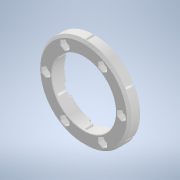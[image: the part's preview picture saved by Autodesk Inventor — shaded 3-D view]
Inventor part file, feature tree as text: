
AUTODESK INVENTOR PART (.ipt)
format: ipt  version: 2020 (Build 240168000, 168)  size: 4,947,968 bytes
history: native  units: in
note: dims shown in document units (in); Inventor stores cm internally (conversion verified against a paired STEP export)
features: extrude x5, sketch x5, other x4, chamfer x2, reference x2, imported_body x1, boolean_combine x1
ambient origin geometry x8: Origin, YZ Plane, XZ Plane, XY Plane, X Axis, Y Axis, Z Axis, Center Point
bodies: Solid1 (feature_tree), Solid2 (feature_tree)
feature tree (20):
  extrude  "Extrusion1"  Depth=0.7in TaperAngle=0.0deg
  extrude  "Extrusion2"  Depth=2.3622in TaperAngle=360.0deg
  imported_body  "Base1"
  boolean_combine  "Combine1"
  extrude  "Extrusion3"  Depth=0.4375in
  extrude  "Extrusion4"  Depth=0.3in TaperAngle=0.0deg
  extrude  "Extrusion5"  Depth=0.0118in TaperAngle=0.0deg
  chamfer  "Chamfer1"  Distance=2.3622in Angle=360.0deg
  chamfer  "Chamfer2"  Distance=0.0118in
  sketch  "Sketch1"  dims[d0=3.5in d2=0.7in d3=0.0in]
  reference  "Reference1"
  sketch  "Sketch2"  dims[d4=0.2656in d5=2.3622in d7=360.0deg]
  reference  "Reference2"
  sketch  "Sketch3"  dims[d9=0.0in d10=0.0in d11=0.4375in]
  sketch  "Sketch4"  dims[d12=2.3622in d14=360.0deg d16=0.3in d17=0.0in]
  sketch  "Sketch5"  dims[d18=2.3622in d20=360.0deg d22=0.0118in d23=0.0in d24=2.3622in d26=360.0deg d28=0.0118in d29=0.0in d30=0.125in d31=0.125in d32=45.0deg d33=0.025in d34=0.125in d35=45.0deg]
  other  "<userpath>\Documents\FRC\2020\Shooter\WheelAndFlywheel2.iam"
  other  "WheelAndFlywheel2.iam"
  other  "6 wheel Rev 4:1"
  other  "TopFlywheelClamp2:1"
